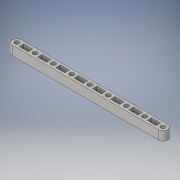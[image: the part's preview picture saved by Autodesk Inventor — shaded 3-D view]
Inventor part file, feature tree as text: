
AUTODESK INVENTOR PART (.ipt)
format: ipt  version: 2016 SP1 (Build 200210100, 210)  size: 189,952 bytes
history: native  units: in
note: dims shown in document units (in); Inventor stores cm internally (conversion verified against a paired STEP export)
features: extrude x3, sketch x3
ambient origin geometry x8: Origin, YZ Plane, XZ Plane, XY Plane, X Axis, Y Axis, Z Axis, Center Point
bodies: Solid1 (feature_tree)
feature tree (6):
  extrude  "Extrusion1"  Depth=0.25in
  extrude  "Extrusion4"  Depth=4.0in
  extrude  "Extrusion5"  Depth=0.5in
  sketch  "Sketch1"  dims[d2=8.0in d3=0.25in]
  sketch  "Sketch4"  dims[d4=0.25in d5=4.0in]
  sketch  "Sketch5"  dims[d6=0.0in d7=0.5in d9=0.25in d10=0.5in d11=0.0in d37=8.0in d45=0.25in d46=4.0in d47=0.0in d48=3.5433in d50=1.0in d51=0.3937in d53=1.0in d55=1.0in d56=0.0in d57=0.5in d58=0.25in d59=3.25in d60=0.125in d61=3.1496in d63=1.0in d64=0.3937in d66=1.0in d68=0.0in d69=0.0in]
